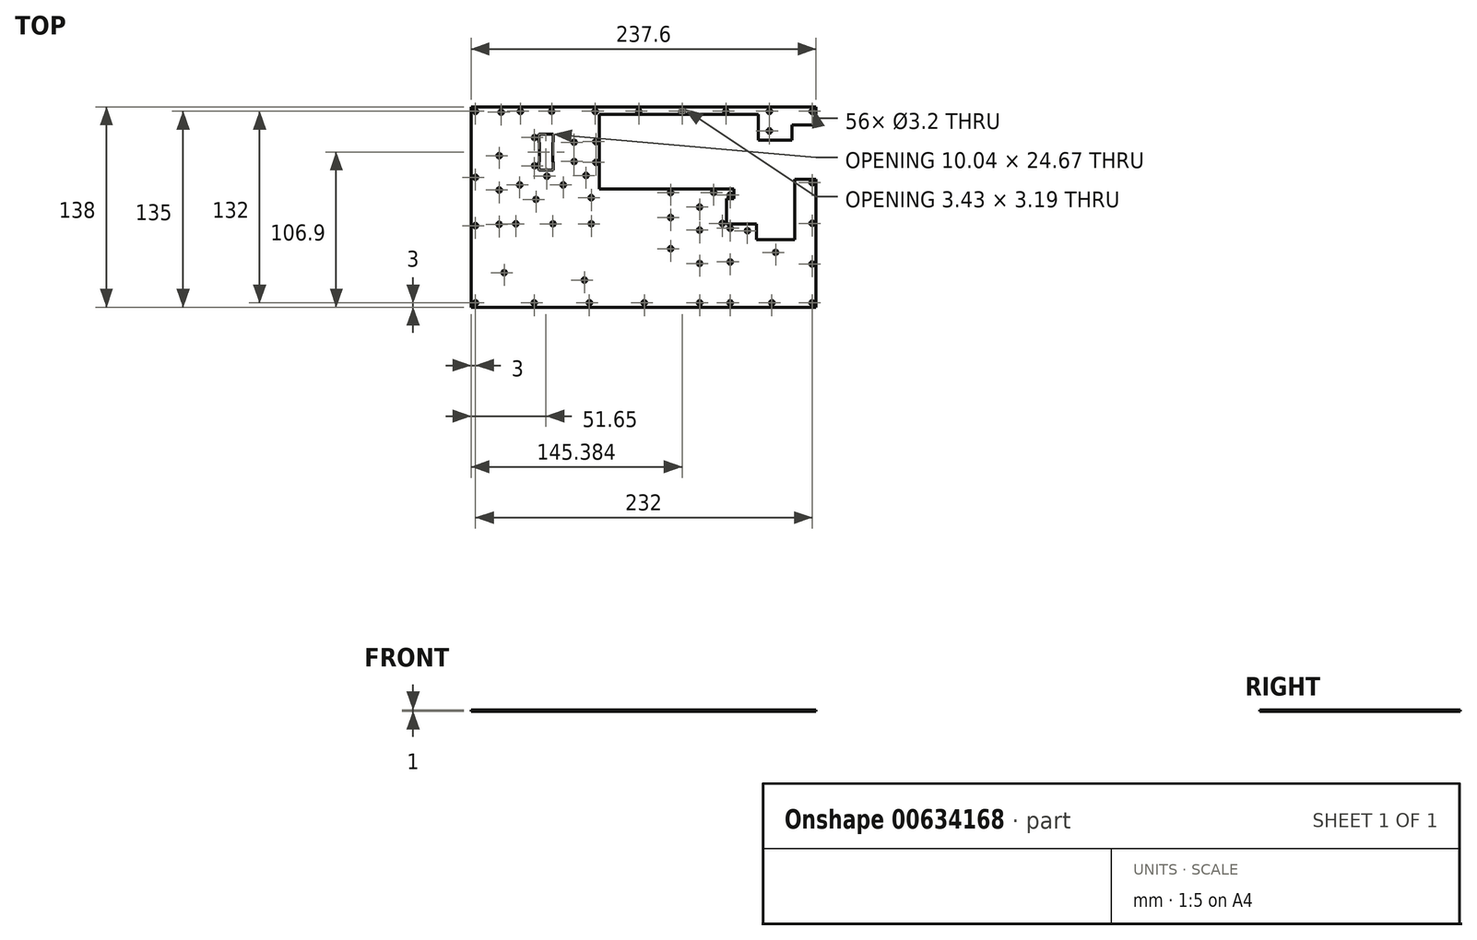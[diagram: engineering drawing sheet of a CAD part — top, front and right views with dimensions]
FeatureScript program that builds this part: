
annotation { "Feature Type Name" : "Feature", "Feature Type Description" : "" }
export const myFeature = defineFeature(function(context is Context, id is Id, definition is map)
    precondition{}
    {
        {
            var Q0;
            Q0=qCreatedBy(makeId("Top.planeOp"),FACE);
            var sketch = newSketch(context, id + "F0", { "sketchPlane" : qUnion([Q0])});
            skArc(sketch, "E0", {"start": v(-72.17, 26.07) * mm, "mid": v(-72.02, 25.71) * mm, "end": v(-71.67, 25.57) * mm});
            skLineSegment(sketch, "E1", {"start": v(-71.67, 25.57) * mm, "end": v(-62.63, 25.57) * mm});
            skArc(sketch, "E2", {"start": v(-62.63, 25.57) * mm, "mid": v(-62.28, 25.71) * mm, "end": v(-62.13, 26.07) * mm});
            skLineSegment(sketch, "E3", {"start": v(-62.13, 26.07) * mm, "end": v(-62.13, 30.67) * mm});
            skArc(sketch, "E4", {"start": v(-62.13, 30.67) * mm, "mid": v(-62.28, 31.02) * mm, "end": v(-62.63, 31.16) * mm});
            skLineSegment(sketch, "E5", {"start": v(-62.63, 31.16) * mm, "end": v(-62.63, 44.64) * mm});
            skArc(sketch, "E6", {"start": v(-62.63, 44.64) * mm, "mid": v(-62.28, 44.78) * mm, "end": v(-62.13, 45.13) * mm});
            skLineSegment(sketch, "E7", {"start": v(-62.13, 45.13) * mm, "end": v(-62.13, 49.73) * mm});
            skArc(sketch, "E8", {"start": v(-62.13, 49.73) * mm, "mid": v(-62.28, 50.09) * mm, "end": v(-62.63, 50.23) * mm});
            skLineSegment(sketch, "E9", {"start": v(-62.63, 50.23) * mm, "end": v(-71.67, 50.23) * mm});
            skArc(sketch, "E10", {"start": v(-71.67, 50.23) * mm, "mid": v(-72.02, 50.09) * mm, "end": v(-72.17, 49.73) * mm});
            skLineSegment(sketch, "E11", {"start": v(-72.17, 49.73) * mm, "end": v(-72.17, 45.13) * mm});
            skArc(sketch, "E12", {"start": v(-72.17, 45.13) * mm, "mid": v(-72.02, 44.78) * mm, "end": v(-71.67, 44.64) * mm});
            skLineSegment(sketch, "E13", {"start": v(-71.67, 44.64) * mm, "end": v(-71.67, 31.16) * mm});
            skArc(sketch, "E14", {"start": v(-71.67, 31.16) * mm, "mid": v(-72.02, 31.02) * mm, "end": v(-72.17, 30.67) * mm});
            skLineSegment(sketch, "E15", {"start": v(-72.17, 30.67) * mm, "end": v(-72.17, 26.07) * mm});
            skLineSegment(sketch, "E16", {"start": v(113.5, 56.7) * mm, "end": v(102.2, 56.7) * mm});
            skLineSegment(sketch, "E17", {"start": v(102.2, 56.7) * mm, "end": v(102.2, 46.28) * mm});
            skLineSegment(sketch, "E18", {"start": v(102.2, 46.28) * mm, "end": v(88.09, 46.28) * mm});
            skLineSegment(sketch, "E19", {"start": v(79, 64) * mm, "end": v(79.01, 63.98) * mm});
            skLineSegment(sketch, "E20", {"start": v(55.07, 64) * mm, "end": v(61.18, 64) * mm});
            skLineSegment(sketch, "E21", {"start": v(61.18, 64) * mm, "end": v(37.36, 64) * mm});
            skLineSegment(sketch, "E22", {"start": v(37.36, 64) * mm, "end": v(37.36, 64) * mm});
            skLineSegment(sketch, "E23", {"start": v(37.38, 12.6) * mm, "end": v(-30.4, 12.6) * mm});
            skLineSegment(sketch, "E24", {"start": v(-30.4, 12.6) * mm, "end": v(-30.4, 64) * mm});
            skLineSegment(sketch, "E25", {"start": v(-30.4, 64) * mm, "end": v(37.36, 64) * mm});
            skLineSegment(sketch, "E26", {"start": v(88.09, 46.28) * mm, "end": v(79.01, 46.28) * mm});
            skLineSegment(sketch, "E27", {"start": v(79.01, 46.28) * mm, "end": v(79, 64) * mm});
            skLineSegment(sketch, "E28", {"start": v(79, 64) * mm, "end": v(61.18, 64) * mm});
            skLineSegment(sketch, "E29", {"start": v(104.2, -22.45) * mm, "end": v(88.88, -22.45) * mm});
            skLineSegment(sketch, "E30", {"start": v(88.88, -22.45) * mm, "end": v(77.8, -22.45) * mm});
            skLineSegment(sketch, "E31", {"start": v(77.8, -22.45) * mm, "end": v(77.8, -11.8) * mm});
            skLineSegment(sketch, "E32", {"start": v(77.8, -11.8) * mm, "end": v(57.15, -11.8) * mm});
            skLineSegment(sketch, "E33", {"start": v(57.15, -11.8) * mm, "end": v(57.15, 5.75) * mm});
            skLineSegment(sketch, "E34", {"start": v(57.15, 5.75) * mm, "end": v(62.2, 5.75) * mm});
            skLineSegment(sketch, "E35", {"start": v(62.2, 5.75) * mm, "end": v(62.2, 12.6) * mm});
            skLineSegment(sketch, "E36", {"start": v(62.2, 12.6) * mm, "end": v(37.38, 12.6) * mm});
            skLineSegment(sketch, "E37", {"start": v(113.55, 19.1) * mm, "end": v(118.8, 19.1) * mm});
            skLineSegment(sketch, "E38", {"start": v(118.8, 19.1) * mm, "end": v(118.8, 19.1) * mm});
            skLineSegment(sketch, "E39", {"start": v(118.8, 19.1) * mm, "end": v(118.8, -69) * mm});
            skLineSegment(sketch, "E40", {"start": v(113.5, 56.7) * mm, "end": v(118.8, 56.7) * mm});
            skLineSegment(sketch, "E41", {"start": v(118.8, 56.7) * mm, "end": v(118.8, 56.7) * mm});
            skLineSegment(sketch, "E42", {"start": v(-118.8, 69) * mm, "end": v(118.8, 69) * mm});
            skLineSegment(sketch, "E43", {"start": v(118.8, 69) * mm, "end": v(118.8, 56.7) * mm});
            skLineSegment(sketch, "E44", {"start": v(113.55, 19.1) * mm, "end": v(104.21, 19.1) * mm});
            skLineSegment(sketch, "E45", {"start": v(104.2, 19.1) * mm, "end": v(104.2, -22.45) * mm});
            skLineSegment(sketch, "E46", {"start": v(-118.8, 69) * mm, "end": v(-118.8, -69) * mm});
            skLineSegment(sketch, "E47", {"start": v(-118.8, -69) * mm, "end": v(118.8, -69) * mm});
            skCircle(sketch, "E48", {"center": v(-115.8, 66) * mm, "radius": 1.6 * mm});
            skCircle(sketch, "E49", {"center": v(-98.1, 65.4) * mm, "radius": 1.6 * mm});
            skCircle(sketch, "E50", {"center": v(-84.8, 66) * mm, "radius": 1.6 * mm});
            skCircle(sketch, "E51", {"center": v(-63.3, 66) * mm, "radius": 1.6 * mm});
            skCircle(sketch, "E52", {"center": v(-99.4, 35.4) * mm, "radius": 1.6 * mm});
            skCircle(sketch, "E53", {"center": v(-75.1, 47.9) * mm, "radius": 1.6 * mm});
            skCircle(sketch, "E54", {"center": v(-47.8, 44.7) * mm, "radius": 1.6 * mm});
            skCircle(sketch, "E55", {"center": v(-75.1, 28.5) * mm, "radius": 1.6 * mm});
            skCircle(sketch, "E56", {"center": v(-66.6, 21.29) * mm, "radius": 1.6 * mm});
            skCircle(sketch, "E57", {"center": v(-47.8, 31.4) * mm, "radius": 1.6 * mm});
            skCircle(sketch, "E58", {"center": v(-115.8, 20.5) * mm, "radius": 1.6 * mm});
            skCircle(sketch, "E59", {"center": v(-99.4, 11.8) * mm, "radius": 1.6 * mm});
            skCircle(sketch, "E60", {"center": v(-85.3, 15.3) * mm, "radius": 1.6 * mm});
            skCircle(sketch, "E61", {"center": v(-55.3, 15.3) * mm, "radius": 1.6 * mm});
            skCircle(sketch, "E62", {"center": v(-32.8, 30.8) * mm, "radius": 1.6 * mm});
            skCircle(sketch, "E63", {"center": v(-32.8, 45.1) * mm, "radius": 1.6 * mm});
            skCircle(sketch, "E64", {"center": v(-33.3, 66) * mm, "radius": 1.6 * mm});
            skCircle(sketch, "E65", {"center": v(-3.3, 66) * mm, "radius": 1.6 * mm});
            skCircle(sketch, "E66", {"center": v(26.47, 66) * mm, "radius": 1.6 * mm});
            skCircle(sketch, "E67", {"center": v(26.7, 66) * mm, "radius": 1.6 * mm});
            skCircle(sketch, "E68", {"center": v(-115.8, -12.8) * mm, "radius": 1.6 * mm});
            skCircle(sketch, "E69", {"center": v(-99.4, -11.9) * mm, "radius": 1.6 * mm});
            skCircle(sketch, "E70", {"center": v(-88, -11.5) * mm, "radius": 1.6 * mm});
            skCircle(sketch, "E71", {"center": v(-62.4, -11.5) * mm, "radius": 1.6 * mm});
            skCircle(sketch, "E72", {"center": v(-36, -11.5) * mm, "radius": 1.6 * mm});
            skCircle(sketch, "E73", {"center": v(-96, -45.2) * mm, "radius": 1.6 * mm});
            skCircle(sketch, "E74", {"center": v(-40.7, -50.3) * mm, "radius": 1.6 * mm});
            skCircle(sketch, "E75", {"center": v(-115.8, -66) * mm, "radius": 1.6 * mm});
            skCircle(sketch, "E76", {"center": v(-75.3, -66) * mm, "radius": 1.6 * mm});
            skCircle(sketch, "E77", {"center": v(-37.3, -66) * mm, "radius": 1.6 * mm});
            skCircle(sketch, "E78", {"center": v(-36, 6.5) * mm, "radius": 1.6 * mm});
            skCircle(sketch, "E79", {"center": v(18.7, 10) * mm, "radius": 1.6 * mm});
            skCircle(sketch, "E80", {"center": v(18.7, -7.2) * mm, "radius": 1.6 * mm});
            skCircle(sketch, "E81", {"center": v(18.7, -28.7) * mm, "radius": 1.6 * mm});
            skCircle(sketch, "E82", {"center": v(0.5, -66) * mm, "radius": 1.6 * mm});
            skCircle(sketch, "E83", {"center": v(38.7, -66) * mm, "radius": 1.6 * mm});
            skCircle(sketch, "E84", {"center": v(59.7, -66) * mm, "radius": 1.6 * mm});
            skCircle(sketch, "E85", {"center": v(38.6, -38.8) * mm, "radius": 1.6 * mm});
            skCircle(sketch, "E86", {"center": v(38.6, -15.9) * mm, "radius": 1.6 * mm});
            skCircle(sketch, "E87", {"center": v(38.6, 0) * mm, "radius": 1.6 * mm});
            skCircle(sketch, "E88", {"center": v(59.7, -14.6) * mm, "radius": 1.6 * mm});
            skCircle(sketch, "E89", {"center": v(54.3, -11.3) * mm, "radius": 1.6 * mm});
            skCircle(sketch, "E90", {"center": v(59.7, -37.8) * mm, "radius": 1.6 * mm});
            skCircle(sketch, "E91", {"center": v(91, -31.2) * mm, "radius": 1.6 * mm});
            skCircle(sketch, "E92", {"center": v(116.2, -39.2) * mm, "radius": 1.6 * mm});
            skCircle(sketch, "E93", {"center": v(116.2, -66) * mm, "radius": 1.6 * mm});
            skCircle(sketch, "E94", {"center": v(88.4, -66) * mm, "radius": 1.6 * mm});
            skCircle(sketch, "E95", {"center": v(116.2, 16.8) * mm, "radius": 1.6 * mm});
            skCircle(sketch, "E96", {"center": v(116.2, -11.2) * mm, "radius": 1.6 * mm});
            skCircle(sketch, "E97", {"center": v(59.7, 8.3) * mm, "radius": 1.6 * mm});
            skCircle(sketch, "E98", {"center": v(48.4, 10.1) * mm, "radius": 1.6 * mm});
            skCircle(sketch, "E99", {"center": v(116.2, 66) * mm, "radius": 1.6 * mm});
            skCircle(sketch, "E100", {"center": v(86.7, 52.5) * mm, "radius": 1.6 * mm});
            skCircle(sketch, "E101", {"center": v(86.7, 66) * mm, "radius": 1.6 * mm});
            skCircle(sketch, "E102", {"center": v(56.7, 66) * mm, "radius": 1.6 * mm});
            skCircle(sketch, "E103", {"center": v(-74.1, 5.3) * mm, "radius": 1.6 * mm});
            skCircle(sketch, "E104", {"center": v(-39.59, 21.8) * mm, "radius": 1.6 * mm});
            skCircle(sketch, "E105", {"center": v(71.6, -16.3) * mm, "radius": 1.6 * mm});
            skLineSegment(sketch, "E106", {"start": v(118.8, -69) * mm, "end": v(118.8, 19.1) * mm});
            skLineSegment(sketch, "E107", {"start": v(118.8, 19.1) * mm, "end": v(104.21, 19.1) * mm});
            skLineSegment(sketch, "E108", {"start": v(104.21, 19.1) * mm, "end": v(104.2, -22.45) * mm});
            skLineSegment(sketch, "E109", {"start": v(104.2, -22.45) * mm, "end": v(77.8, -22.45) * mm});
            skLineSegment(sketch, "E110", {"start": v(62.2, 12.6) * mm, "end": v(-30.4, 12.6) * mm});
            skLineSegment(sketch, "E111", {"start": v(-30.4, 64) * mm, "end": v(79, 64) * mm});
            skLineSegment(sketch, "E112", {"start": v(79, 64) * mm, "end": v(79.01, 46.28) * mm});
            skLineSegment(sketch, "E113", {"start": v(79.01, 46.28) * mm, "end": v(102.2, 46.28) * mm});
            skLineSegment(sketch, "E114", {"start": v(102.2, 46.28) * mm, "end": v(102.2, 56.7) * mm});
            skLineSegment(sketch, "E115", {"start": v(102.2, 56.7) * mm, "end": v(118.8, 56.7) * mm});
            skLineSegment(sketch, "E116", {"start": v(118.8, 56.7) * mm, "end": v(118.8, 69) * mm});
            skLineSegment(sketch, "E117", {"start": v(118.8, 69) * mm, "end": v(-118.8, 69) * mm});
            skSolve(sketch);
        }
        {
            var Q0;
            Q0=makeQuery(id+"F0.imprint","IMPRINT",FACE,{"disambiguationData":[TD([[makeQuery(id+"F0.imprint","IMPRINT",EDGE,{"derivedFrom":sQuery(id+"F0.wireOp",EDGE,"E0")}),-1.0]])]});
            extrude(context, id + "F1", {"entities" : qUnion([Q0]), "depth" : 1 * mm, "offsetDistance" : 25 * mm});
        }
    });
